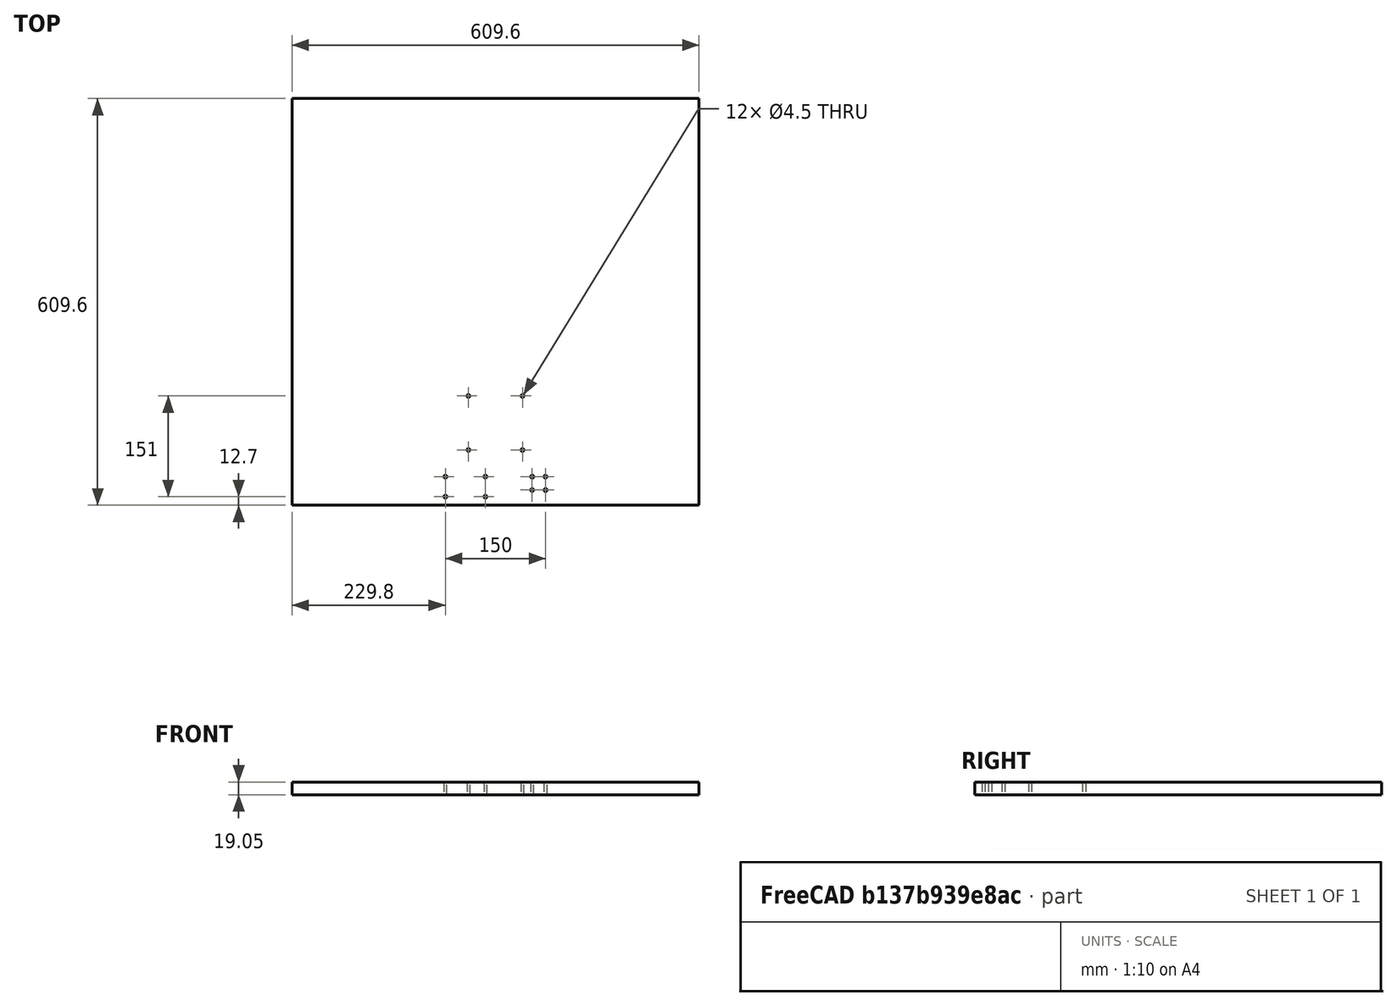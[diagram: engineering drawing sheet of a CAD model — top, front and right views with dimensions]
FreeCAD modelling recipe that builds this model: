
FCSTD DOCUMENT  (FreeCAD 0.19R22665 (Git))
Label: plywood base assembly
License: All rights reserved
LicenseURL: http://en.wikipedia.org/wiki/All_rights_reserved
objects: TechDraw::DrawViewDimension×13, App::Link×6, PartDesign::CoordinateSystem×5, App::DocumentObjectGroup×2, App::Part×2, TechDraw::DrawSVGTemplate×2, TechDraw::DrawProjGroupItem×2, TechDraw::DrawProjGroup×2, TechDraw::DrawPage×2, Sketcher::SketchObject×1, PartDesign::Pad×1, App::FeaturePython×1, PartDesign::Body×1, TechDraw::DrawViewDetail×1
note: 9 computed .brp shape members not serialized (recipe doc carries the construction recipe); baked Part::Feature solids carry a one-line shape summary decoded from their .brp
EXTERNAL_REF file=A4.FCStd obj=LCS_0
EXTERNAL_REF file=A4.FCStd obj=RISER_1_0
EXTERNAL_REF file=PCB-BRACKET-1.0.FCStd obj=base
EXTERNAL_REF file=PCB-BRACKET-1.0.FCStd obj=Body
EXTERNAL_REF file=PCB-BRACKET-B-1.0.FCStd obj=base
EXTERNAL_REF file=PCB-BRACKET-B-1.0.FCStd obj=Body
EXTERNAL_REF file=Arduino Mega.FCStd obj=LCS_1
EXTERNAL_REF file=PCB-BRACKET-1.0.FCStd obj=arduino
EXTERNAL_REF file=Arduino Mega.FCStd obj=Arduino_Mega
EXTERNAL_REF file=Arduino Mega.FCStd obj=pcb
EXTERNAL_REF file=PCB-1.0.FCStd obj=LCS_1
EXTERNAL_REF file=PCB-1.0.FCStd obj=Body

FEATURE [Sketcher::SketchObject] Sketch
  MapMode = 5
  Support = -> [XY_Plane]
  sketch-geometry (28):
    g0: LineSegment [constr] StartX=-40.5 StartY=40.5 StartZ=0 EndX=40.5 EndY=40.5 EndZ=0
    g1: LineSegment [constr] StartX=40.5 StartY=40.5 StartZ=0 EndX=40.5 EndY=-40.5 EndZ=0
    g2: LineSegment [constr] StartX=40.5 StartY=-40.5 StartZ=0 EndX=-40.5 EndY=-40.5 EndZ=0
    g3: LineSegment [constr] StartX=-40.5 StartY=-40.5 StartZ=0 EndX=-40.5 EndY=40.5 EndZ=0
    g4: Circle CenterX=-40.5 CenterY=40.5 CenterZ=0 NormalX=0 NormalY=0 NormalZ=1 AngleXU=0 Radius=2.25
    g5: Circle CenterX=40.5 CenterY=40.5 CenterZ=0 NormalX=0 NormalY=0 NormalZ=1 AngleXU=0 Radius=2.25
    g6: Circle CenterX=40.5 CenterY=-40.5 CenterZ=0 NormalX=0 NormalY=0 NormalZ=1 AngleXU=0 Radius=2.25
    g7: Circle CenterX=-40.5 CenterY=-40.5 CenterZ=0 NormalX=0 NormalY=0 NormalZ=1 AngleXU=0 Radius=2.25
    g8: LineSegment [constr] StartX=-75 StartY=-80.5 StartZ=0 EndX=-15 EndY=-80.5 EndZ=0
    g9: LineSegment [constr] StartX=-15 StartY=-80.5 StartZ=0 EndX=-15 EndY=-110.5 EndZ=0
    g10: LineSegment [constr] StartX=-15 StartY=-110.5 StartZ=0 EndX=-75 EndY=-110.5 EndZ=0
    g11: LineSegment [constr] StartX=-75 StartY=-110.5 StartZ=0 EndX=-75 EndY=-80.5 EndZ=0
    g12: Circle CenterX=-75 CenterY=-80.5 CenterZ=0 NormalX=0 NormalY=0 NormalZ=1 AngleXU=0 Radius=2.25
    g13: Circle CenterX=-15 CenterY=-80.5 CenterZ=0 NormalX=0 NormalY=0 NormalZ=1 AngleXU=0 Radius=2.25
    g14: Circle CenterX=-15 CenterY=-110.5 CenterZ=0 NormalX=0 NormalY=0 NormalZ=1 AngleXU=0 Radius=2.25
    g15: Circle CenterX=-75 CenterY=-110.5 CenterZ=0 NormalX=0 NormalY=0 NormalZ=1 AngleXU=0 Radius=2.25
    g16: LineSegment [constr] StartX=55 StartY=-80.5 StartZ=0 EndX=75 EndY=-80.5 EndZ=0
    g17: LineSegment [constr] StartX=75 StartY=-80.5 StartZ=0 EndX=75 EndY=-100.5 EndZ=0
    g18: LineSegment [constr] StartX=75 StartY=-100.5 StartZ=0 EndX=55 EndY=-100.5 EndZ=0
    g19: LineSegment [constr] StartX=55 StartY=-100.5 StartZ=0 EndX=55 EndY=-80.5 EndZ=0
    g20: Circle CenterX=55 CenterY=-80.5 CenterZ=0 NormalX=0 NormalY=0 NormalZ=1 AngleXU=0 Radius=2.25
    g21: Circle CenterX=75 CenterY=-80.5 CenterZ=0 NormalX=0 NormalY=0 NormalZ=1 AngleXU=0 Radius=2.25
    g22: Circle CenterX=75 CenterY=-100.5 CenterZ=0 NormalX=0 NormalY=0 NormalZ=1 AngleXU=0 Radius=2.25
    g23: Circle CenterX=55 CenterY=-100.5 CenterZ=0 NormalX=0 NormalY=0 NormalZ=1 AngleXU=0 Radius=2.25
    g24: LineSegment StartX=-304.8 StartY=-123.2 StartZ=0 EndX=304.8 EndY=-123.2 EndZ=0
    g25: LineSegment StartX=304.8 StartY=-123.2 StartZ=0 EndX=304.8 EndY=486.4 EndZ=0
    g26: LineSegment StartX=304.8 StartY=486.4 StartZ=0 EndX=-304.8 EndY=486.4 EndZ=0
    g27: LineSegment StartX=-304.8 StartY=486.4 StartZ=0 EndX=-304.8 EndY=-123.2 EndZ=0
  constraints (68):
    c: Coincident(g0,g1)
    c: Coincident(g1,g2)
    c: Coincident(g2,g3)
    c: Coincident(g3,g0)
    c: Horizontal(g2)
    c: Vertical(g1)
    c: Coincident(g4,g0)
    c: Coincident(g5,g0)
    c: Coincident(g6,g1)
    c: Coincident(g7,g2)
    c: Equal(g3,g0)
    c: DistanceX(g0,g0) = 81
    c: Diameter(g6) = 4.5
    c: Equal(g6,g7)
    c: Equal(g7,g4)
    c: Equal(g4,g5)
    c: Symmetric(g4,g5,g-2)
    c: Symmetric(g4,g7,g-1)
    c: Coincident(g8,g9)
    c: Coincident(g9,g10)
    c: Coincident(g10,g11)
    c: Coincident(g11,g8)
    c: Horizontal(g8)
    c: Horizontal(g10)
    c: Vertical(g9)
    c: Vertical(g11)
    c: Coincident(g12,g8)
    c: Coincident(g13,g8)
    c: Coincident(g14,g9)
    c: Coincident(g15,g10)
    c: Equal(g15,g12)
    c: Equal(g12,g13)
    c: Equal(g13,g14)
    c: Equal(g14,g7)
    c: DistanceX(g8,g8) = 60
    c: DistanceY(g11,g11) = 30
    c: DistanceY(g13,g7) = 40
    c: Coincident(g16,g17)
    c: Coincident(g17,g18)
    c: Coincident(g18,g19)
    c: Coincident(g19,g16)
    c: Horizontal(g16)
    c: Horizontal(g18)
    c: Vertical(g17)
    c: Vertical(g19)
    c: Coincident(g20,g16)
    c: Coincident(g21,g16)
    c: Coincident(g22,g17)
    c: Coincident(g23,g18)
    c: Equal(g23,g22)
    c: Equal(g22,g21)
    c: Equal(g21,g20)
    c: Equal(g13,g20)
    c: Equal(g16,g19)
    c: DistanceX(g16,g16) = 20
    c: DistanceX(g13,g20) = 70
    c: Symmetric(g12,g21,g-2)
    c: Coincident(g24,g25)
    c: Coincident(g25,g26)
    c: Coincident(g26,g27)
    c: Coincident(g27,g24)
    c: Horizontal(g24)
    c: Vertical(g25)
    c: Vertical(g27)
    c: Equal(g27,g26)
    c: Symmetric(g26,g25,g-2)
    c: DistanceY(g25,g25) = 609.6
    c: DistanceY(g24,g15) = 12.7
FEATURE [PartDesign::Pad] Pad
  Direction = (1,1,1)
  Length = 19.05
  Length2 = 100
  Profile = -> Sketch
  Refine = true
  Type = 0
FEATURE [PartDesign::CoordinateSystem] LCS_Origin
  AttacherType = Attacher::AttachEngine3D
  MapMode = 2
  Support = -> [X_Axis001]
FEATURE [App::DocumentObjectGroup] Constraints
FEATURE [App::FeaturePython] Variables  label="var"  # WARN: FeaturePython — macro-defined, semantics opaque (R4)
  plywoodT = 12.7
FEATURE [App::Link] A4_RISER_1_0
  AssemblyType = Asm4EE
  AttachedBy = #LCS_0
  AttachedTo = plywood_base#LCS_1
  LinkPlacement = pos=(-3e-16,1e-16,0) rot=(0,0,1;0rad)
  LinkedObject = -> <external A4.FCStd>#RISER_1_0
  Placement = pos=(-3e-16,1e-16,0) rot=(0,0,1;0rad)
  expr: Placement = plywood_base.Placement * LCS_1.Placement * AttachmentOffset * A4#LCS_0.Placement ^ -1
FEATURE [App::Link] plywood_base  label="plywood_base_1"
  AssemblyType = Asm4EE
  AttachedBy = #LCS_1
  AttachedTo = Parent Assembly#LCS_Origin
  LinkPlacement = pos=(-1.21e-14,-4e-15,-19.05) rot=(0,0,1;0rad)
  LinkedObject = -> Body
  Placement = pos=(-1.21e-14,-4e-15,-19.05) rot=(0,0,1;0rad)
  expr: Placement = LCS_Origin.Placement * AttachmentOffset * LCS_1.Placement ^ -1
FEATURE [PartDesign::CoordinateSystem] LCS_1
  AttacherType = Attacher::AttachEngine3D
  MapMode = 45
  Placement = pos=(1.21e-14,4e-15,19.05) rot=(0,0,1;0rad)
  Support = -> [Pad]
FEATURE [PartDesign::CoordinateSystem] pcb
  AttacherType = Attacher::AttachEngine3D
  MapMode = 11
  Placement = pos=(-75,-80.5,19.05) rot=(0,0,1;1.5708rad)
  Support = -> [Pad]
FEATURE [PartDesign::CoordinateSystem] pcb_b
  AttacherType = Attacher::AttachEngine3D
  MapMode = 11
  Placement = pos=(55,-80.5,19.05) rot=(0,0,1;1.5708rad)
  Support = -> [Pad]
FEATURE [PartDesign::Body] Body  label="plywood_base_body"
  Group = -> [Sketch,Pad,LCS_1,pcb,pcb_b]
  Origin = -> Origin
  Tip = -> Pad
FEATURE [App::Link] PCB_BRACKET_1_0
  AssemblyType = Asm4EE
  AttachedBy = #base
  AttachedTo = plywood_base#pcb
  LinkPlacement = pos=(-85,-70.5,4) rot=(0,0,1;0rad)
  LinkedObject = -> <external PCB-BRACKET-1.0.FCStd>#Body
  Placement = pos=(-85,-70.5,4) rot=(0,0,1;0rad)
  expr: Placement = plywood_base.Placement * pcb.Placement * AttachmentOffset * PCB_BRACKET_1_0#base.Placement ^ -1
FEATURE [App::Link] PCB_BRACKET_B_1_0
  AssemblyType = Asm4EE
  AttachedBy = #base
  AttachedTo = plywood_base#pcb_b
  LinkPlacement = pos=(45,-70.5,4) rot=(0,0,1;0rad)
  LinkedObject = -> <external PCB-BRACKET-B-1.0.FCStd>#Body
  Placement = pos=(45,-70.5,4) rot=(0,0,1;0rad)
  expr: Placement = plywood_base.Placement * pcb_b.Placement * AttachmentOffset * PCB_BRACKET_B_1_0#base.Placement ^ -1
FEATURE [App::Link] Arduino_Mega
  AssemblyType = Asm4EE
  AttachedBy = #LCS_1
  AttachedTo = PCB_BRACKET_1_0#arduino
  LinkPlacement = pos=(-48.3224,-94.6681,8.651) rot=(0,-1,0;3.14159rad)
  LinkedObject = -> <external Arduino Mega.FCStd>#Arduino_Mega
  Placement = pos=(-48.3224,-94.6681,8.651) rot=(0,-1,0;3.14159rad)
  expr: Placement = PCB_BRACKET_1_0.Placement * PCB_BRACKET_1_0#arduino.Placement * AttachmentOffset * Arduino_Mega#LCS_1.Placement ^ -1
FEATURE [App::Link] PCB_1_0
  AssemblyType = Asm4EE
  AttachedBy = #LCS_1
  AttachedTo = Arduino_Mega#pcb
  AttachmentOffset = pos=(0,0,-2.54) rot=(-1,0,0;3.14159rad)
  LinkPlacement = pos=(-89.7736,-53.0619,19.7508) rot=(0,0,1;0rad)
  LinkedObject = -> <external PCB-1.0.FCStd>#Body
  Placement = pos=(-89.7736,-53.0619,19.7508) rot=(0,0,1;0rad)
  expr: Placement = Arduino_Mega.Placement * Arduino_Mega#pcb.Placement * AttachmentOffset * PCB_1_0#LCS_1.Placement ^ -1
FEATURE [App::Part] Model
  Configuration = 0
  Group = -> [LCS_Origin,Constraints,Variables,A4_RISER_1_0,plywood_base,PCB_BRACKET_1_0,PCB_BRACKET_B_1_0,Arduino_Mega,PCB_1_0]
  Origin = -> Origin001
  Type = Assembly4 Model
FEATURE [PartDesign::CoordinateSystem] LCS_0
  AttacherType = Attacher::AttachEngine3D
  MapMode = 2
  Support = -> [X_Axis002]
FEATURE [App::Part] plywood_base001  label="plywood_base"
  Group = -> [LCS_0,Body]
  Origin = -> Origin002
FEATURE [App::DocumentObjectGroup] Parts
  Group = -> [plywood_base001]
FEATURE [TechDraw::DrawSVGTemplate] Template
  EditableTexts = AUTHOR_NAME=CARL WINGE; DRAWING_TITLE=PLYWOOD BASE; PN=PLYWOOD-BASE-1.0
  Height = 215.9
  Orientation = 1
  Width = 279.4
FEATURE [TechDraw::DrawProjGroupItem] ProjItem  label="Front"
  CoarseView = false
  Direction = (0,0,1)
  Focus = 100
  HardHidden = false
  IsoCount = 0
  IsoHidden = false
  IsoVisible = false
  LockPosition = true
  Perspective = false
  Rotation = 0
  RotationVector = (1,0,0)
  Scale = 0.1
  ScaleType = 2
  SeamHidden = false
  SeamVisible = true
  SmoothHidden = false
  SmoothVisible = true
  Source = -> [plywood_base001]
  Type = 0
  X = 0
  XDirection = (1,0,0)
  Y = 0
FEATURE [TechDraw::DrawProjGroup] ProjGroup
  Anchor = -> ProjItem
  AutoDistribute = true
  LockPosition = false
  ProjectionType = 1
  Rotation = 0
  Scale = 0.1
  ScaleType = 2
  Source = -> [plywood_base001]
  Views = -> [ProjItem]
  X = 53.9895
  Y = 164.183
  spacingX = 15
  spacingY = 15
FEATURE [TechDraw::DrawViewDimension] Dimension
  Arbitrary = false
  FormatSpec = %.1f
  Inverted = false
  LockPosition = false
  MeasureType = 1
  OverTolerance = 0
  References2D = -> [ProjItem]
  Rotation = 0
  ScaleType = 0
  TheoreticalExact = false
  Type = 1
  UnderTolerance = 0
  X = -18.99
  Y = -38.2393
FEATURE [TechDraw::DrawViewDimension] Dimension001
  Arbitrary = false
  FormatSpec = %.1f
  Inverted = false
  LockPosition = false
  MeasureType = 1
  OverTolerance = 0
  References2D = -> [ProjItem]
  Rotation = 0
  ScaleType = 0
  TheoreticalExact = false
  Type = 1
  UnderTolerance = 0
  X = 3.64836
  Y = -51.1637
FEATURE [TechDraw::DrawViewDimension] Dimension002
  Arbitrary = false
  FormatSpec = %.1f
  Inverted = false
  LockPosition = false
  MeasureType = 1
  OverTolerance = 0
  References2D = -> [ProjItem]
  Rotation = 0
  ScaleType = 0
  TheoreticalExact = false
  Type = 2
  UnderTolerance = 0
  X = 36.2692
  Y = 1.4473
FEATURE [TechDraw::DrawViewDetail] Detail
  AnchorPoint = (5,-240,0)
  BaseView = -> ProjItem
  CoarseView = false
  Direction = (0,0,1)
  Focus = 100
  HardHidden = false
  IsoCount = 0
  IsoHidden = false
  IsoVisible = false
  LockPosition = false
  Perspective = false
  Radius = 150
  Reference = 1
  Rotation = 0
  Scale = 0.3
  ScaleType = 2
  SeamHidden = false
  SeamVisible = true
  SmoothHidden = false
  SmoothVisible = true
  Source = -> [plywood_base001]
  X = 179.001
  XDirection = (1,0,0)
  Y = 117.639
FEATURE [TechDraw::DrawViewDimension] Dimension003
  Arbitrary = false
  FormatSpec = %.1f
  Inverted = false
  LockPosition = false
  MeasureType = 1
  OverTolerance = 0
  References2D = -> [Detail]
  Rotation = 0
  ScaleType = 0
  TheoreticalExact = false
  Type = 1
  UnderTolerance = 0
  X = -14.5177
  Y = -23.6382
FEATURE [TechDraw::DrawViewDimension] Dimension004
  Arbitrary = false
  FormatSpec = %.1f
  Inverted = false
  LockPosition = false
  MeasureType = 1
  OverTolerance = 0
  References2D = -> [Detail]
  Rotation = 0
  ScaleType = 0
  TheoreticalExact = false
  Type = 2
  UnderTolerance = 0
  X = -32.0739
  Y = 2.55744
FEATURE [TechDraw::DrawViewDimension] Dimension005
  Arbitrary = false
  FormatSpec = %.1f
  Inverted = false
  LockPosition = false
  MeasureType = 1
  OverTolerance = 0
  References2D = -> [Detail]
  Rotation = 0
  ScaleType = 0
  TheoreticalExact = false
  Type = 2
  UnderTolerance = 0
  X = -21.3622
  Y = 10.7037
FEATURE [TechDraw::DrawViewDimension] Dimension006
  Arbitrary = false
  FormatSpec = %.1f
  Inverted = false
  LockPosition = false
  MeasureType = 1
  OverTolerance = 0
  References2D = -> [Detail]
  Rotation = 0
  ScaleType = 0
  TheoreticalExact = false
  Type = 2
  UnderTolerance = 0
  X = 24.2263
  Y = 1.70271
FEATURE [TechDraw::DrawViewDimension] Dimension007
  Arbitrary = false
  FormatSpec = %.1f
  Inverted = false
  LockPosition = false
  MeasureType = 1
  OverTolerance = 0
  References2D = -> [Detail]
  Rotation = 0
  ScaleType = 0
  TheoreticalExact = false
  Type = 1
  UnderTolerance = 0
  X = 8.55709
  Y = -24.8306
FEATURE [TechDraw::DrawViewDimension] Dimension008
  Arbitrary = false
  FormatSpec = %.1f
  Inverted = false
  LockPosition = false
  MeasureType = 1
  OverTolerance = 0
  References2D = -> [Detail]
  Rotation = 0
  ScaleType = 0
  TheoreticalExact = false
  Type = 1
  UnderTolerance = 0
  X = 3.75
  Y = -11.775
FEATURE [TechDraw::DrawViewDimension] Dimension009
  Arbitrary = false
  FormatSpec = %.1f
  Inverted = false
  LockPosition = false
  MeasureType = 1
  OverTolerance = 0
  References2D = -> [Detail]
  Rotation = 0
  ScaleType = 0
  TheoreticalExact = false
  Type = 1
  UnderTolerance = 0
  X = -1.25
  Y = 24.725
FEATURE [TechDraw::DrawViewDimension] Dimension010
  Arbitrary = false
  FormatSpec = %.1f
  Inverted = false
  LockPosition = false
  MeasureType = 1
  OverTolerance = 0
  References2D = -> [Detail]
  Rotation = 0
  ScaleType = 0
  TheoreticalExact = false
  Type = 2
  UnderTolerance = 0
  X = 13.7046
  Y = 15.2037
FEATURE [TechDraw::DrawViewDimension] Dimension011
  Arbitrary = false
  FormatSpec = %.1f
  Inverted = false
  LockPosition = false
  MeasureType = 1
  OverTolerance = 0
  References2D = -> [Detail]
  Rotation = 0
  ScaleType = 0
  TheoreticalExact = false
  Type = 1
  UnderTolerance = 0
  X = 1.71311
  Y = 2.01052
FEATURE [TechDraw::DrawViewDimension] Dimension012
  Arbitrary = false
  FormatSpec = %.1f
  Inverted = false
  LockPosition = false
  MeasureType = 1
  OverTolerance = 0
  References2D = -> [Detail]
  Rotation = 0
  ScaleType = 0
  TheoreticalExact = false
  Type = 2
  UnderTolerance = 0
  X = -41.0672
  Y = -24.1092
FEATURE [TechDraw::DrawPage] Page
  KeepUpdated = true
  NextBalloonIndex = 1
  ProjectionType = 1
  Template = -> Template
  Views = -> [ProjGroup,Dimension,Dimension001,Dimension002,Detail,Dimension003,Dimension004,Dimension005,Dimension006,Dimension007,Dimension008,Dimension009,Dimension010,Dimension011,Dimension012]
FEATURE [TechDraw::DrawSVGTemplate] Template001
  EditableTexts = AUTHOR_NAME=CARL WINGE; DRAWING_TITLE=BASE 1:1; PN=BASE-1.0
  Height = 215.9
  Orientation = 1
  Width = 279.4
FEATURE [TechDraw::DrawProjGroupItem] ProjItem001  label="Front001"
  CoarseView = false
  Direction = (0,0,1)
  Focus = 100
  HardHidden = false
  IsoCount = 0
  IsoHidden = false
  IsoVisible = false
  LockPosition = true
  Perspective = false
  Rotation = 0
  RotationVector = (-1,0,0)
  ScaleType = 2
  SeamHidden = false
  SeamVisible = true
  SmoothHidden = false
  SmoothVisible = true
  Source = -> [Pad]
  Type = 0
  X = 0
  XDirection = (1,1e-16,0)
  Y = 0
FEATURE [TechDraw::DrawProjGroup] ProjGroup001
  Anchor = -> ProjItem001
  AutoDistribute = true
  LockPosition = false
  ProjectionType = 1
  Rotation = 0
  ScaleType = 0
  Source = -> [Pad]
  Views = -> [ProjItem001]
  X = 139.7
  Y = 338.434
  spacingX = 15
  spacingY = 15
FEATURE [TechDraw::DrawPage] Page001
  KeepUpdated = true
  NextBalloonIndex = 1
  ProjectionType = 1
  Template = -> Template001
  Views = -> [ProjGroup001]

RESOLVED EXTERNAL PARTS (link-assembly join: the EXTERNAL_REF files above that resolve inside this repo's crawl, each included once):
---- part A4.FCStd = doc fcstd_4f0d3c391a03 (162005 chars; too large to inline — full recipe in that document) ----
---- part PCB-1.0.FCStd = doc fcstd_699dace254ec ----
FCSTD DOCUMENT  (FreeCAD 0.19R22665 (Git))
Label: PCB-1.0
License: All rights reserved
LicenseURL: http://en.wikipedia.org/wiki/All_rights_reserved
objects: Sketcher::SketchObject×1, PartDesign::Pad×1, PartDesign::CoordinateSystem×1, PartDesign::Body×1
note: 5 computed .brp shape members not serialized (recipe doc carries the construction recipe); baked Part::Feature solids carry a one-line shape summary decoded from their .brp

FEATURE [Sketcher::SketchObject] Sketch001
  MapMode = 5
  Support = -> [XY_Plane]
  sketch-geometry (5):
    g0: LineSegment StartX=0 StartY=0 StartZ=0 EndX=120 EndY=0 EndZ=0
    g1: LineSegment StartX=120 StartY=0 StartZ=0 EndX=120 EndY=-70 EndZ=0
    g2: LineSegment StartX=120 StartY=-70 StartZ=0 EndX=0 EndY=-70 EndZ=0
    g3: LineSegment StartX=0 StartY=-70 StartZ=0 EndX=0 EndY=0 EndZ=0
    g4: Circle CenterX=13.2 CenterY=-17.4 CenterZ=0 NormalX=0 NormalY=0 NormalZ=1 AngleXU=0 Radius=0.5
  constraints (14):
    c: Coincident(g0,g1)
    c: Coincident(g1,g2)
    c: Coincident(g2,g3)
    c: Coincident(g3,g0)
    c: Horizontal(g0)
    c: Horizontal(g2)
    c: Vertical(g1)
    c: Vertical(g3)
    c: Coincident(g0,g-1)
    c: DistanceX(g0,g0) = 120
    c: DistanceY(g1,g1) = 70
    c: Diameter(g4) = 1
    c: DistanceX(g0,g4) = 13.2
    c: DistanceY(g4,g0) = 17.4
FEATURE [PartDesign::Pad] Pad
  Direction = (1,1,1)
  Length = 1.6
  Length2 = 100
  Profile = -> Sketch001
  Refine = true
  Type = 0
FEATURE [PartDesign::CoordinateSystem] LCS_1
  AttacherType = Attacher::AttachEngine3D
  MapMode = 11
  Placement = pos=(13.2,-17.4,0) rot=(0,0,1;1.5708rad)
  Support = -> [Pad]
FEATURE [PartDesign::Body] Body  label="PCB"
  Group = -> [Sketch001,Pad,LCS_1]
  Origin = -> Origin
  Tip = -> Pad
---- part PCB-BRACKET-1.0.FCStd = doc fcstd_c4c7f8b29682 ----
FCSTD DOCUMENT  (FreeCAD 0.19R22665 (Git))
Label: PCB-BRACKET-1.0
License: All rights reserved
LicenseURL: http://en.wikipedia.org/wiki/All_rights_reserved
objects: Sketcher::SketchObject×2, PartDesign::Pad×2, PartDesign::CoordinateSystem×2, PartDesign::Body×1
note: 9 computed .brp shape members not serialized (recipe doc carries the construction recipe); baked Part::Feature solids carry a one-line shape summary decoded from their .brp

FEATURE [Sketcher::SketchObject] Sketch
  MapMode = 5
  Support = -> [XY_Plane]
  sketch-geometry (16):
    g0: Circle CenterX=0 CenterY=0 CenterZ=0 NormalX=0 NormalY=0 NormalZ=1 AngleXU=0 Radius=1.5
    g1: Circle CenterX=-1.3 CenterY=-48.2 CenterZ=0 NormalX=0 NormalY=0 NormalZ=1 AngleXU=0 Radius=1.5
    g2: Circle CenterX=74.9 CenterY=0 CenterZ=0 NormalX=0 NormalY=0 NormalZ=1 AngleXU=0 Radius=1.5
    g3: Circle CenterX=79.98 CenterY=-48.2 CenterZ=0 NormalX=0 NormalY=0 NormalZ=1 AngleXU=0 Radius=1.5
    g4: LineSegment [constr] StartX=10 StartY=-10 StartZ=0 EndX=70 EndY=-10 EndZ=0
    g5: LineSegment [constr] StartX=70 StartY=-10 StartZ=0 EndX=70 EndY=-40 EndZ=0
    g6: LineSegment [constr] StartX=70 StartY=-40 StartZ=0 EndX=10 EndY=-40 EndZ=0
    g7: LineSegment [constr] StartX=10 StartY=-40 StartZ=0 EndX=10 EndY=-10 EndZ=0
    g8: Circle CenterX=10 CenterY=-10 CenterZ=0 NormalX=0 NormalY=0 NormalZ=1 AngleXU=0 Radius=2.75
    g9: Circle CenterX=70 CenterY=-10 CenterZ=0 NormalX=0 NormalY=0 NormalZ=1 AngleXU=0 Radius=2.75
    g10: Circle CenterX=70 CenterY=-40 CenterZ=0 NormalX=0 NormalY=0 NormalZ=1 AngleXU=0 Radius=2.75
    g11: Circle CenterX=10 CenterY=-40 CenterZ=0 NormalX=0 NormalY=0 NormalZ=1 AngleXU=0 Radius=2.75
    g12: LineSegment StartX=-6.3 StartY=5 StartZ=0 EndX=84.98 EndY=5 EndZ=0
    g13: LineSegment StartX=84.98 StartY=5 StartZ=0 EndX=84.98 EndY=-53.2 EndZ=0
    g14: LineSegment StartX=84.98 StartY=-53.2 StartZ=0 EndX=-6.3 EndY=-53.2 EndZ=0
    g15: LineSegment StartX=-6.3 StartY=-53.2 StartZ=0 EndX=-6.3 EndY=5 EndZ=0
  constraints (43):
    c: Coincident(g0,g-1)
    c: PointOnObject(g2,g-1)
    c: Diameter(g1) = 3
    c: Equal(g1,g3)
    c: Equal(g1,g2)
    c: Equal(g1,g0)
    c: DistanceX(g0,g2) = 74.9
    c: DistanceX(g1,g0) = 1.3
    c: DistanceY(g1,g0) = 48.2
    c: Horizontal(g3,g1)
    c: DistanceX(g1,g3) = 81.28
    c: Coincident(g4,g5)
    c: Coincident(g5,g6)
    c: Coincident(g6,g7)
    c: Coincident(g7,g4)
    c: Horizontal(g4)
    c: Horizontal(g6)
    c: Vertical(g5)
    c: Vertical(g7)
    c: DistanceX(g4,g4) = 60
    c: DistanceY(g7,g7) = 30
    c: Coincident(g8,g4)
    c: Coincident(g9,g4)
    c: Coincident(g10,g5)
    c: Coincident(g11,g6)
    c: Diameter(g8) = 5.5
    c: Equal(g8,g9)
    c: Equal(g8,g10)
    c: Equal(g8,g11)
    c: DistanceY(g8,g-1) = 10
    c: DistanceX(g-1,g8) = 10
    c: Coincident(g12,g13)
    c: Coincident(g13,g14)
    c: Coincident(g14,g15)
    c: Coincident(g15,g12)
    c: Horizontal(g12)
    c: Horizontal(g14)
    c: Vertical(g13)
    c: Vertical(g15)
    c: DistanceY(g0,g12) = 5
    c: DistanceX(g14,g1) = 5
    c: DistanceY(g14,g1) = 5
    c: DistanceX(g3,g13) = 5
FEATURE [PartDesign::Pad] Pad
  Direction = (1,1,1)
  Length = 3
  Length2 = 100
  Profile = -> Sketch
  Type = 0
FEATURE [Sketcher::SketchObject] Sketch001
  MapMode = 5
  Support = -> [XY_Plane]
  sketch-geometry (12):
    g0: LineSegment [constr] StartX=10 StartY=-10 StartZ=0 EndX=70 EndY=-10 EndZ=0
    g1: LineSegment [constr] StartX=70 StartY=-10 StartZ=0 EndX=70 EndY=-40 EndZ=0
    g2: LineSegment [constr] StartX=70 StartY=-40 StartZ=0 EndX=10 EndY=-40 EndZ=0
    g3: LineSegment [constr] StartX=10 StartY=-40 StartZ=0 EndX=10 EndY=-10 EndZ=0
    g4: Circle CenterX=10 CenterY=-10 CenterZ=0 NormalX=0 NormalY=0 NormalZ=1 AngleXU=0 Radius=5
    g5: Circle CenterX=10 CenterY=-10 CenterZ=0 NormalX=0 NormalY=0 NormalZ=1 AngleXU=0 Radius=2.75
    g6: Circle CenterX=70 CenterY=-10 CenterZ=0 NormalX=0 NormalY=0 NormalZ=1 AngleXU=0 Radius=5
    g7: Circle CenterX=70 CenterY=-10 CenterZ=0 NormalX=0 NormalY=0 NormalZ=1 AngleXU=0 Radius=2.75
    g8: Circle CenterX=70 CenterY=-40 CenterZ=0 NormalX=0 NormalY=0 NormalZ=1 AngleXU=0 Radius=5
    g9: Circle CenterX=70 CenterY=-40 CenterZ=0 NormalX=0 NormalY=0 NormalZ=1 AngleXU=0 Radius=2.75
    g10: Circle CenterX=10 CenterY=-40 CenterZ=0 NormalX=0 NormalY=0 NormalZ=1 AngleXU=0 Radius=5
    g11: Circle CenterX=10 CenterY=-40 CenterZ=0 NormalX=0 NormalY=0 NormalZ=1 AngleXU=0 Radius=2.75
  constraints (28):
    c: Coincident(g0,g1)
    c: Coincident(g1,g2)
    c: Coincident(g2,g3)
    c: Coincident(g3,g0)
    c: Horizontal(g0)
    c: Horizontal(g2)
    c: Vertical(g1)
    c: Vertical(g3)
    c: DistanceX(g0,g0) = 60
    c: DistanceY(g3,g3) = 30
    c: DistanceY(g0,g-1) = 10
    c: DistanceX(g-1,g0) = 10
    c: Coincident(g4,g0)
    c: Coincident(g5,g4)
    c: Coincident(g6,g0)
    c: Coincident(g7,g6)
    c: Coincident(g8,g1)
    c: Coincident(g9,g8)
    c: Coincident(g10,g2)
    c: Coincident(g11,g10)
    c: Diameter(g11) = 5.5
    c: Equal(g11,g5)
    c: Equal(g11,g7)
    c: Equal(g11,g9)
    c: Equal(g8,g6)
    c: Equal(g6,g4)
    c: Equal(g4,g10)
    c: Diameter(g10) = 10
FEATURE [PartDesign::Pad] Pad001
  BaseFeature = -> Pad
  Direction = (1,1,1)
  Length = 4
  Length2 = 100
  Profile = -> Sketch001
  Reversed = true
  Type = 0
FEATURE [PartDesign::CoordinateSystem] base
  AttacherType = Attacher::AttachEngine3D
  MapMode = 11
  Placement = pos=(10,-10,-4) rot=(0,0,1;1.5708rad)
  Support = -> [Pad001]
FEATURE [PartDesign::CoordinateSystem] arduino
  AttacherType = Attacher::AttachEngine3D
  MapMode = 11
  Placement = pos=(0,0,3) rot=(0,0,1;1.5708rad)
  Support = -> [Pad001]
FEATURE [PartDesign::Body] Body
  Group = -> [Sketch,Pad,Sketch001,Pad001,base,arduino]
  Origin = -> Origin
  Tip = -> Pad001
---- part PCB-BRACKET-B-1.0.FCStd = doc fcstd_66dbba682f3b ----
FCSTD DOCUMENT  (FreeCAD 0.19R22665 (Git))
Label: PCB-BRACKET-B-1.0
License: All rights reserved
LicenseURL: http://en.wikipedia.org/wiki/All_rights_reserved
objects: Sketcher::SketchObject×2, PartDesign::Pad×2, PartDesign::CoordinateSystem×1, PartDesign::Body×1
note: 8 computed .brp shape members not serialized (recipe doc carries the construction recipe); baked Part::Feature solids carry a one-line shape summary decoded from their .brp

FEATURE [Sketcher::SketchObject] Sketch
  MapMode = 5
  Support = -> [XY_Plane]
  sketch-geometry (20):
    g0: LineSegment [constr] StartX=10 StartY=-10 StartZ=0 EndX=30 EndY=-10 EndZ=0
    g1: LineSegment [constr] StartX=30 StartY=-10 StartZ=0 EndX=30 EndY=-30 EndZ=0
    g2: LineSegment [constr] StartX=30 StartY=-30 StartZ=0 EndX=10 EndY=-30 EndZ=0
    g3: LineSegment [constr] StartX=10 StartY=-30 StartZ=0 EndX=10 EndY=-10 EndZ=0
    g4: Circle CenterX=10 CenterY=-10 CenterZ=0 NormalX=0 NormalY=0 NormalZ=1 AngleXU=0 Radius=2.75
    g5: Circle CenterX=30 CenterY=-10 CenterZ=0 NormalX=0 NormalY=0 NormalZ=1 AngleXU=0 Radius=2.75
    g6: Circle CenterX=30 CenterY=-30 CenterZ=0 NormalX=0 NormalY=0 NormalZ=1 AngleXU=0 Radius=2.75
    g7: Circle CenterX=10 CenterY=-30 CenterZ=0 NormalX=0 NormalY=0 NormalZ=1 AngleXU=0 Radius=2.75
    g8: LineSegment StartX=-5 StartY=5 StartZ=0 EndX=41.8 EndY=5 EndZ=0
    g9: LineSegment StartX=41.8 StartY=5 StartZ=0 EndX=41.8 EndY=-41.8 EndZ=0
    g10: LineSegment StartX=41.8 StartY=-41.8 StartZ=0 EndX=-5 EndY=-41.8 EndZ=0
    g11: LineSegment StartX=-5 StartY=-41.8 StartZ=0 EndX=-5 EndY=5 EndZ=0
    g12: Circle CenterX=0 CenterY=0 CenterZ=0 NormalX=0 NormalY=0 NormalZ=1 AngleXU=0 Radius=1.5
    g13: Circle CenterX=36.8 CenterY=0 CenterZ=0 NormalX=0 NormalY=0 NormalZ=1 AngleXU=0 Radius=1.5
    g14: Circle CenterX=0 CenterY=-36.8 CenterZ=0 NormalX=0 NormalY=0 NormalZ=1 AngleXU=0 Radius=1.5
    g15: Circle CenterX=36.8 CenterY=-36.8 CenterZ=0 NormalX=0 NormalY=0 NormalZ=1 AngleXU=0 Radius=1.5
    g16: LineSegment [constr] StartX=0 StartY=0 StartZ=0 EndX=36.8 EndY=0 EndZ=0
    g17: LineSegment [constr] StartX=36.8 StartY=0 StartZ=0 EndX=36.8 EndY=-36.8 EndZ=0
    g18: LineSegment [constr] StartX=36.8 StartY=-36.8 StartZ=0 EndX=0 EndY=-36.8 EndZ=0
    g19: LineSegment [constr] StartX=0 StartY=-36.8 StartZ=0 EndX=0 EndY=0 EndZ=0
  constraints (51):
    c: Coincident(g0,g1)
    c: Coincident(g1,g2)
    c: Coincident(g2,g3)
    c: Coincident(g3,g0)
    c: Horizontal(g0)
    c: Horizontal(g2)
    c: Vertical(g1)
    c: Vertical(g3)
    c: DistanceX(g0,g0) = 20
    c: DistanceY(g3,g3) = 20
    c: Coincident(g4,g0)
    c: Coincident(g5,g0)
    c: Coincident(g6,g1)
    c: Coincident(g7,g2)
    c: Diameter(g4) = 5.5
    c: Equal(g4,g5)
    c: Equal(g4,g6)
    c: Equal(g4,g7)
    c: DistanceY(g4,g-1) = 10
    c: DistanceX(g-1,g4) = 10
    c: Coincident(g8,g9)
    c: Coincident(g9,g10)
    c: Coincident(g10,g11)
    c: Coincident(g11,g8)
    c: Horizontal(g8)
    c: Horizontal(g10)
    c: Vertical(g9)
    c: PointOnObject(g13,g-1)
    c: Coincident(g16,g17)
    c: Coincident(g17,g18)
    c: Coincident(g18,g19)
    c: Coincident(g19,g16)
    c: Horizontal(g18)
    c: Vertical(g17)
    c: Vertical(g19)
    c: Coincident(g16,g12)
    c: Coincident(g17,g15)
    c: Coincident(g13,g16)
    c: Coincident(g14,g18)
    c: Diameter(g14) = 3
    c: Equal(g14,g15)
    c: Equal(g14,g13)
    c: Equal(g14,g12)
    c: Equal(g16,g19)
    c: DistanceX(g16,g16) = 36.8
    c: DistanceX(g15,g9) = 5
    c: Coincident(g12,g-1)
    c: DistanceY(g9,g15) = 5
    c: DistanceX(g8,g12) = 5
    c: Vertical(g11)
    c: DistanceY(g13,g8) = 5
FEATURE [PartDesign::Pad] Pad
  Direction = (1,1,1)
  Length = 3
  Length2 = 100
  Profile = -> Sketch
  Type = 0
FEATURE [Sketcher::SketchObject] Sketch001
  MapMode = 5
  Support = -> [XY_Plane]
  sketch-geometry (12):
    g0: LineSegment [constr] StartX=10 StartY=-10 StartZ=0 EndX=30 EndY=-10 EndZ=0
    g1: LineSegment [constr] StartX=30 StartY=-10 StartZ=0 EndX=30 EndY=-30 EndZ=0
    g2: LineSegment [constr] StartX=30 StartY=-30 StartZ=0 EndX=10 EndY=-30 EndZ=0
    g3: LineSegment [constr] StartX=10 StartY=-30 StartZ=0 EndX=10 EndY=-10 EndZ=0
    g4: Circle CenterX=10 CenterY=-10 CenterZ=0 NormalX=0 NormalY=0 NormalZ=1 AngleXU=0 Radius=2.75
    g5: Circle CenterX=30 CenterY=-10 CenterZ=0 NormalX=0 NormalY=0 NormalZ=1 AngleXU=0 Radius=2.75
    g6: Circle CenterX=30 CenterY=-10 CenterZ=0 NormalX=0 NormalY=0 NormalZ=1 AngleXU=0 Radius=5
    g7: Circle CenterX=10 CenterY=-10 CenterZ=0 NormalX=0 NormalY=0 NormalZ=1 AngleXU=0 Radius=5
    g8: Circle CenterX=10 CenterY=-30 CenterZ=0 NormalX=0 NormalY=0 NormalZ=1 AngleXU=0 Radius=2.75
    g9: Circle CenterX=10 CenterY=-30 CenterZ=0 NormalX=0 NormalY=0 NormalZ=1 AngleXU=0 Radius=5
    g10: Circle CenterX=30 CenterY=-30 CenterZ=0 NormalX=0 NormalY=0 NormalZ=1 AngleXU=0 Radius=2.75
    g11: Circle CenterX=30 CenterY=-30 CenterZ=0 NormalX=0 NormalY=0 NormalZ=1 AngleXU=0 Radius=5
  constraints (28):
    c: Coincident(g0,g1)
    c: Coincident(g1,g2)
    c: Coincident(g2,g3)
    c: Coincident(g3,g0)
    c: Horizontal(g0)
    c: Horizontal(g2)
    c: Vertical(g1)
    c: Vertical(g3)
    c: DistanceY(g0,g-1) = 10
    c: DistanceX(g-1,g0) = 10
    c: Equal(g0,g3)
    c: DistanceX(g0,g0) = 20
    c: Coincident(g4,g0)
    c: Coincident(g5,g0)
    c: Coincident(g6,g5)
    c: Coincident(g7,g4)
    c: Coincident(g8,g2)
    c: Coincident(g9,g8)
    c: Coincident(g10,g1)
    c: Coincident(g11,g10)
    c: Equal(g11,g6)
    c: Equal(g6,g7)
    c: Equal(g7,g9)
    c: Diameter(g9) = 10
    c: Diameter(g4) = 5.5
    c: Equal(g4,g5)
    c: Equal(g4,g10)
    c: Equal(g4,g8)
FEATURE [PartDesign::Pad] Pad001
  BaseFeature = -> Pad
  Direction = (1,1,1)
  Length = 4
  Length2 = 100
  Profile = -> Sketch001
  Reversed = true
  Type = 0
FEATURE [PartDesign::CoordinateSystem] base
  AttacherType = Attacher::AttachEngine3D
  MapMode = 11
  Placement = pos=(10,-10,-4) rot=(0,0,1;1.5708rad)
  Support = -> [Pad001]
FEATURE [PartDesign::Body] Body
  Group = -> [Sketch,Pad,Sketch001,Pad001,base]
  Origin = -> Origin
  Tip = -> Pad001
